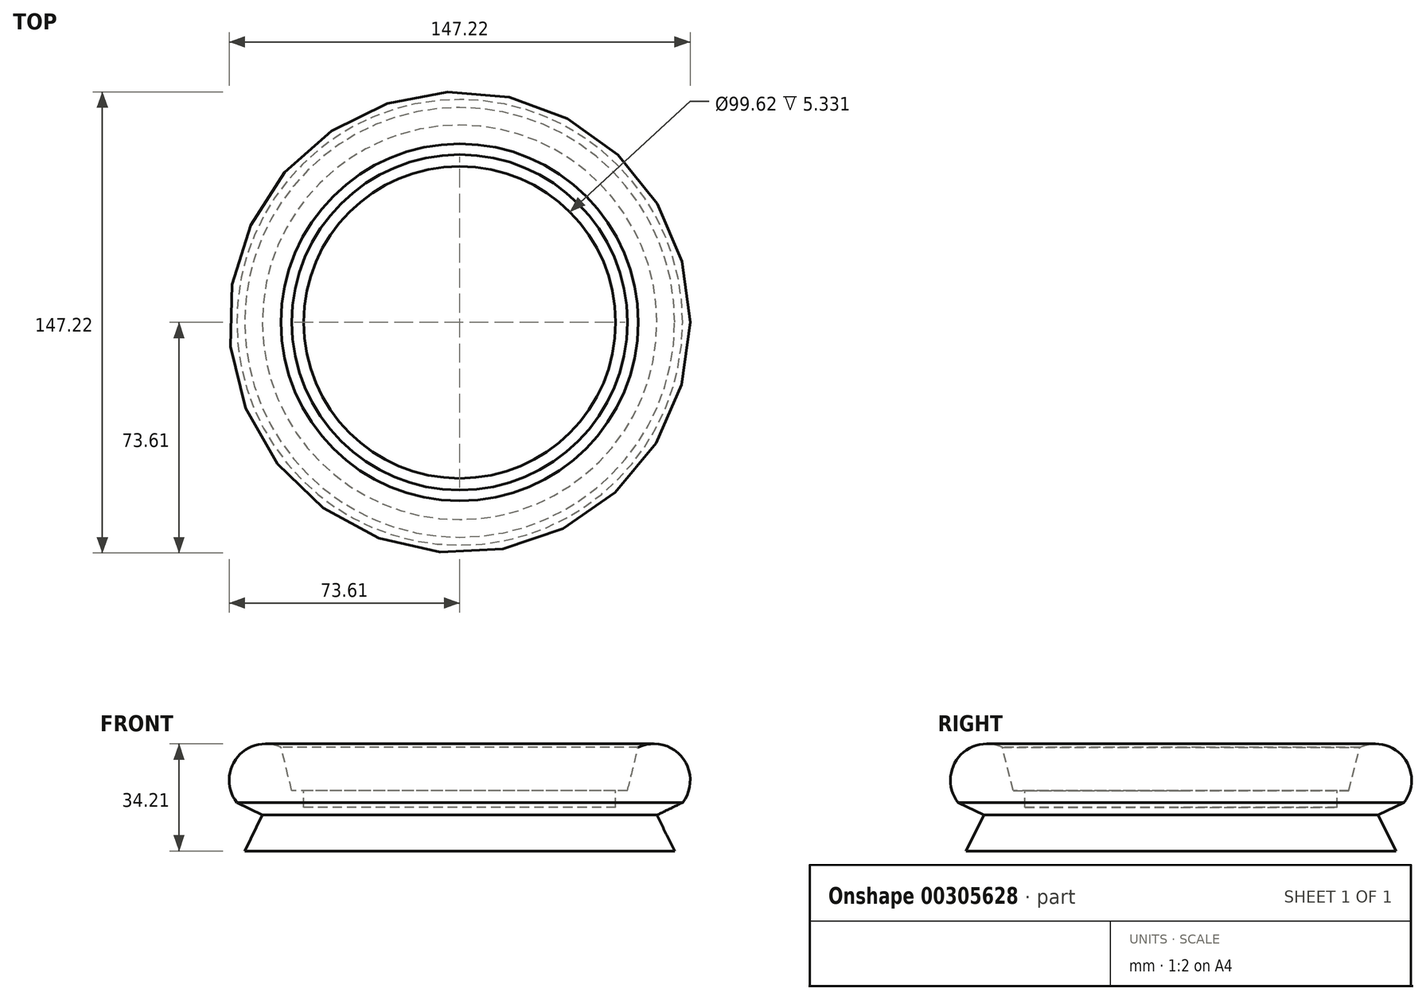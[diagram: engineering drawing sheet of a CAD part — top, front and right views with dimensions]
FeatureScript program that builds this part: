
annotation { "Feature Type Name" : "Feature", "Feature Type Description" : "" }
export const myFeature = defineFeature(function(context is Context, id is Id, definition is map)
    precondition{}
    {
        {
            var Q0;
            Q0=qCreatedBy(makeId("Front.planeOp"),FACE);
            var sketch = newSketch(context, id + "F0", { "sketchPlane" : qUnion([Q0])});
            skLineSegment(sketch, "E0", {"start": v(0, 0) * mm, "end": v(68.63, 0) * mm});
            skLineSegment(sketch, "E1", {"start": v(68.63, 0) * mm, "end": v(62.98, 11.45) * mm});
            skLineSegment(sketch, "E2", {"start": v(62.98, 11.45) * mm, "end": v(71.16, 15.48) * mm});
            skArc(sketch, "E3", {"start": v(71.16, 15.48) * mm, "mid": v(71.06, 29.87) * mm, "end": v(57.02, 33.08) * mm});
            skLineSegment(sketch, "E4", {"start": v(57.02, 33.08) * mm, "end": v(53.58, 19.28) * mm});
            skLineSegment(sketch, "E5", {"start": v(53.58, 19.28) * mm, "end": v(49.81, 19.28) * mm});
            skLineSegment(sketch, "E6", {"start": v(49.81, 19.28) * mm, "end": v(49.81, 13.95) * mm});
            skLineSegment(sketch, "E7", {"start": v(49.81, 13.95) * mm, "end": v(0, 13.95) * mm});
            skLineSegment(sketch, "E8", {"start": v(0, 13.95) * mm, "end": v(0, 0) * mm});
            skSolve(sketch);
        }
        {
            var Q0;
            Q0 = qSketchRegion(id + "F0", true);
            var Q1;
            Q1=sQuery(id+"F0.wireOp",EDGE,"E8");
            revolve(context, id + "F1", {"entities" : qUnion([Q0]), "axis" : qUnion([Q1]), "revolveType" : RevolveType.FULL});
        }
    });
